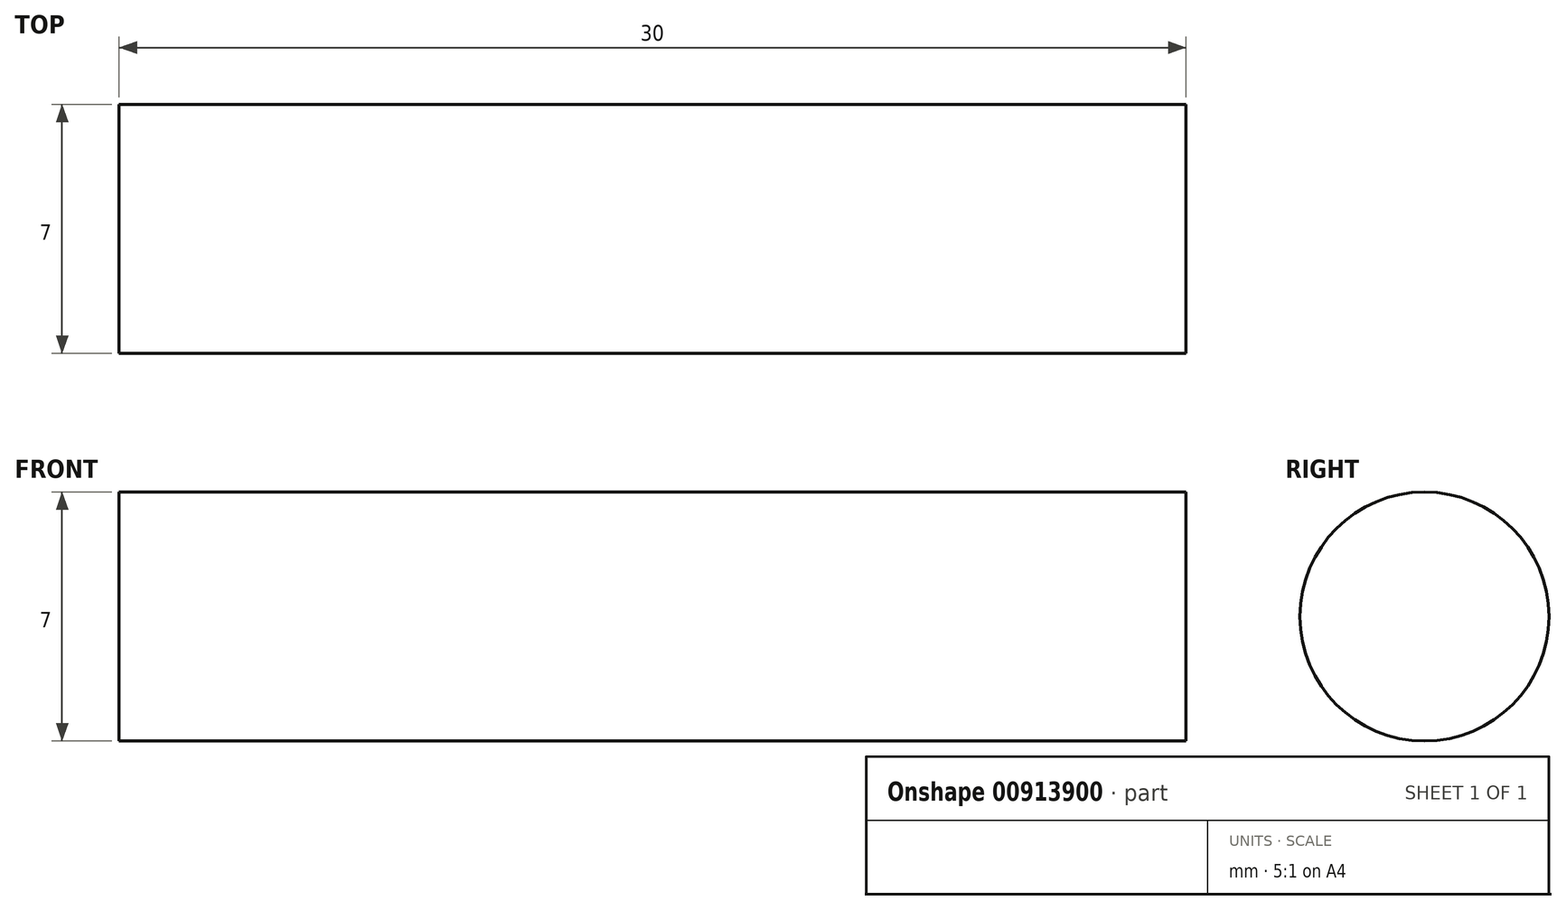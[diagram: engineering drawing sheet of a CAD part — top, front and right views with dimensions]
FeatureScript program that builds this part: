
annotation { "Feature Type Name" : "Feature", "Feature Type Description" : "" }
export const myFeature = defineFeature(function(context is Context, id is Id, definition is map)
    precondition{}
    {
        {
            var Q0;
            Q0=qCreatedBy(makeId("Right.planeOp"),FACE);
            var sketch = newSketch(context, id + "F0", { "sketchPlane" : qUnion([Q0])});
            skCircle(sketch, "E0", {"center": v(0, 0) * mm, "radius": 3.5 * mm});
            skSolve(sketch);
        }
        {
            var Q0;
            Q0=makeQuery(id+"F0.imprint","IMPRINT",FACE,{"disambiguationData":[TD([[makeQuery(id+"F0.imprint","IMPRINT",EDGE,{"derivedFrom":sQuery(id+"F0.wireOp",EDGE,"E0")}),1.0]])]});
            extrude(context, id + "F1", {"entities" : qUnion([Q0]), "depth" : 30 * mm, "offsetDistance" : 25 * mm});
        }
    });
